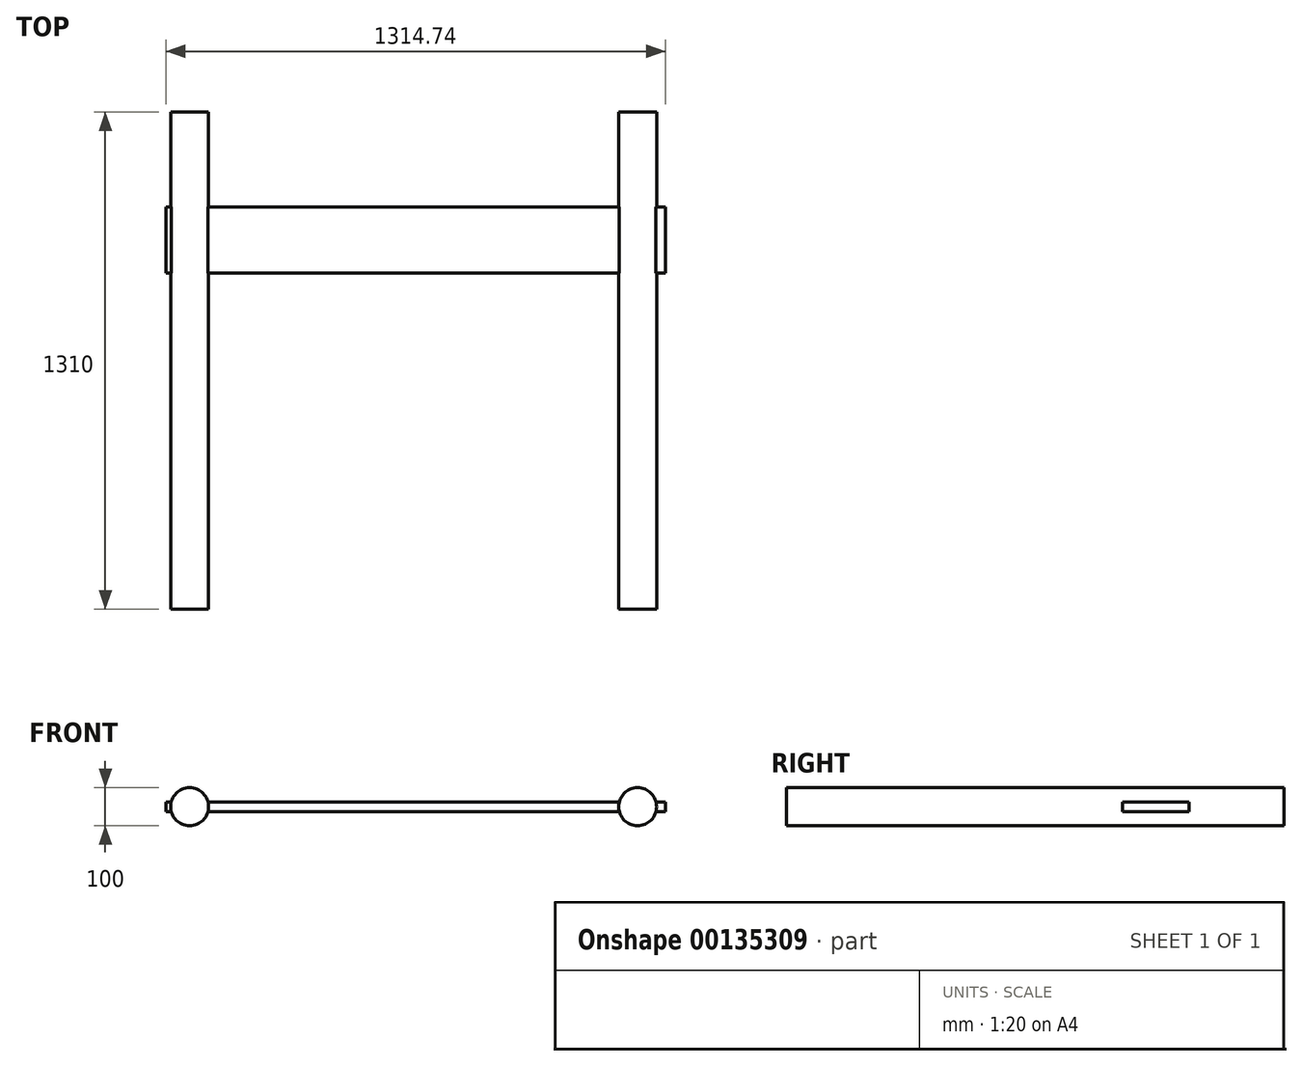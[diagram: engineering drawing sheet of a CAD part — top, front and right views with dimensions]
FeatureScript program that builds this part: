
annotation { "Feature Type Name" : "Feature", "Feature Type Description" : "" }
export const myFeature = defineFeature(function(context is Context, id is Id, definition is map)
    precondition{}
    {
        {
            var Q0;
            Q0=qCreatedBy(makeId("Front.planeOp"),FACE);
            var sketch = newSketch(context, id + "F0", { "sketchPlane" : qUnion([Q0])});
            skCircle(sketch, "E0", {"center": v(590, 0) * mm, "radius": 50 * mm});
            skCircle(sketch, "E1", {"center": v(-590, 0) * mm, "radius": 50 * mm});
            skLineSegment(sketch, "E2", {"start": v(0, 0) * mm, "end": v(0, 357.57) * mm, "construction": true});
            skSolve(sketch);
        }
        {
            var Q0;
            Q0 = qSketchRegion(id + "F0", true);
            extrude(context, id + "F1", {"entities" : qUnion([Q0]), "depth" : 1310 * mm, "symmetric" : true});
        }
        {
            var Q0;
            Q0=qCreatedBy(makeId("Top.planeOp"),FACE);
            var sketch = newSketch(context, id + "F2", { "sketchPlane" : qUnion([Q0])});
            skLineSegment(sketch, "E3.bottom", {"start": v(-651.96, 404.88) * mm, "end": v(662.78, 404.88) * mm});
            skLineSegment(sketch, "E3.top", {"start": v(-651.96, 229.95) * mm, "end": v(662.78, 229.95) * mm});
            skLineSegment(sketch, "E3.left", {"start": v(-651.96, 404.88) * mm, "end": v(-651.96, 229.95) * mm});
            skLineSegment(sketch, "E3.right", {"start": v(662.78, 404.88) * mm, "end": v(662.78, 229.95) * mm});
            skSolve(sketch);
        }
        {
            var Q0;
            Q0 = qSketchRegion(id + "F2", true);
            extrude(context, id + "F3", {"entities" : qUnion([Q0]), "operationType" : NewBodyOperationType.ADD, "depth" : 25 * mm, "symmetric" : true});
        }
    });
